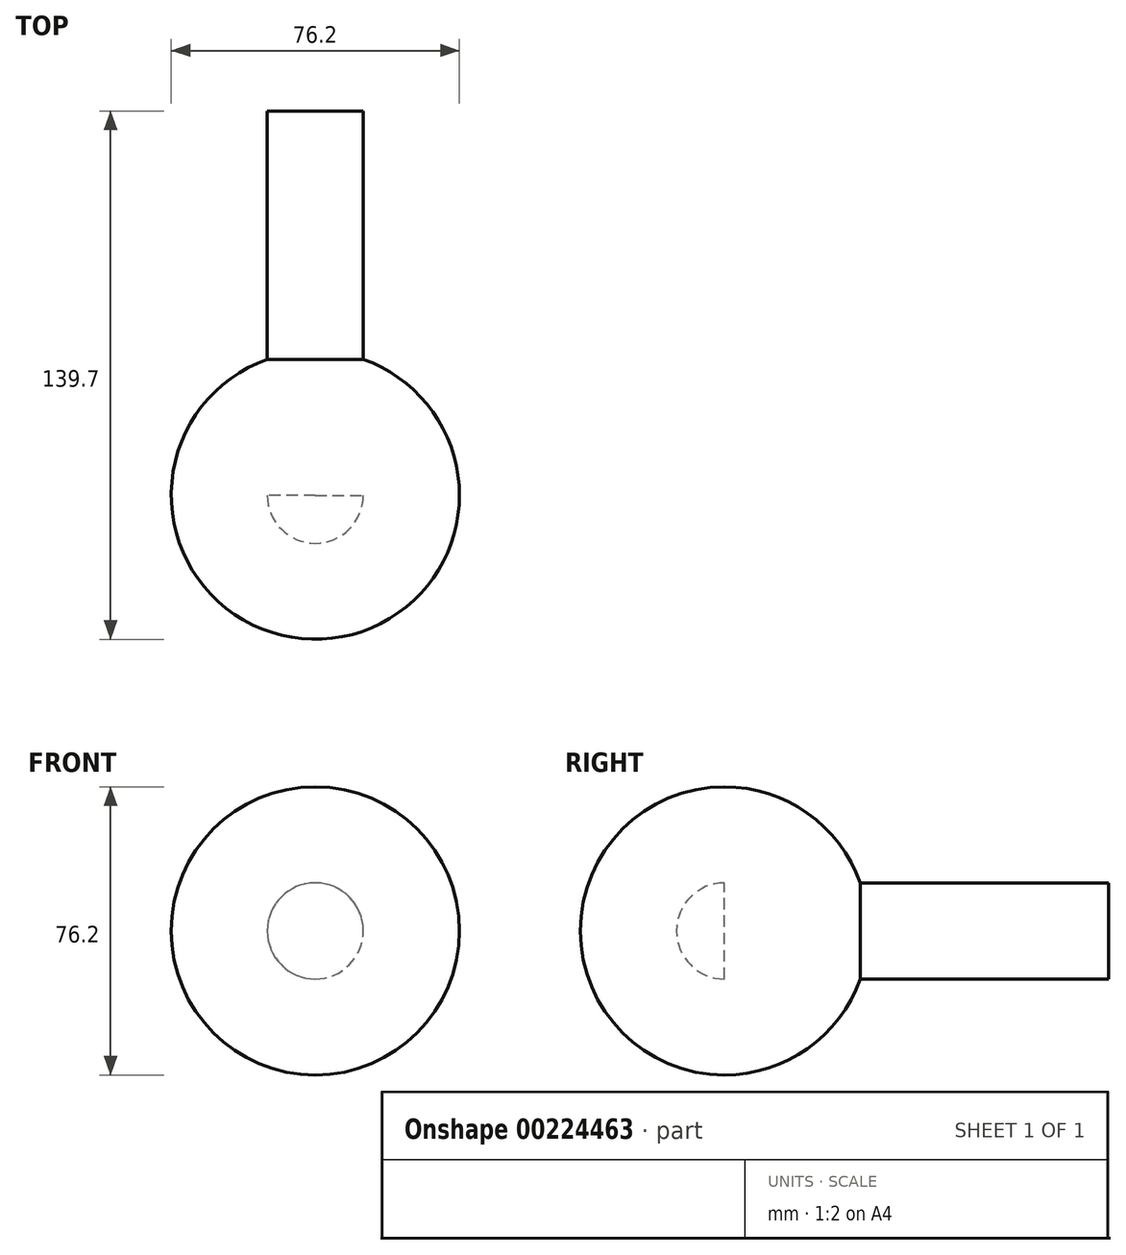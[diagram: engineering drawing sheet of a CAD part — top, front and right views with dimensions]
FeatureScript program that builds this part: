
annotation { "Feature Type Name" : "Feature", "Feature Type Description" : "" }
export const myFeature = defineFeature(function(context is Context, id is Id, definition is map)
    precondition{}
    {
        {
            var Q0;
            Q0=qCreatedBy(makeId("Front.planeOp"),FACE);
            var sketch = newSketch(context, id + "F0", { "sketchPlane" : qUnion([Q0])});
            skCircle(sketch, "E0", {"center": v(0, 0) * mm, "radius": 12.7 * mm});
            skSolve(sketch);
        }
        {
            var Q0;
            Q0 = qSketchRegion(id + "F0", true);
            extrude(context, id + "F1", {"entities" : qUnion([Q0]), "depth" : 101.6 * mm});
        }
        {
            var Q0;
            Q0=makeQuery(id+"F1.opExtrude","CAP_FACE",FACE,{"disambiguationData":[OSD([sQuery(id+"F0.wireOp",EDGE,"E0")])],"isStart":false});
            var sketch = newSketch(context, id + "F2", { "sketchPlane" : qUnion([Q0])});
            skCircle(sketch, "E1", {"center": v(0, 0) * mm, "radius": 38.1 * mm});
            skLineSegment(sketch, "E2", {"start": v(0, 38.1) * mm, "end": v(0, -38.1) * mm});
            skSolve(sketch);
        }
        {
            var Q0;
            {var subQ0=sQuery(id+"F2.wireOp",EDGE,"E2");var subQ1=sQuery(id+"F2.wireOp",EDGE,"E1");var subQ2=makeQuery(id+"F2.imprint","INTERSECT",VERTEX,{"disambiguationData":[OD(0.0)],"derivedFrom":[subQ1,subQ0]});Q0=makeQuery(id+"F2.imprint","IMPRINT",FACE,{"disambiguationData":[TD([[makeQuery(id+"F2.imprint","IMPRINT",EDGE,{"disambiguationData":[TD([[subQ2,1.0]])],"derivedFrom":subQ1}),1.0]])]});}
            var Q1;
            {var subQ0=sQuery(id+"F2.wireOp",EDGE,"E2");var subQ1=makeQuery(id+"F1.opExtrude","CAP_EDGE",EDGE,{"disambiguationData":[OSD([sQuery(id+"F0.wireOp",EDGE,"E0")])],"isStart":false});var subQ2=makeQuery(id+"F2.imprint","INTERSECT",VERTEX,{"disambiguationData":[OD(0.0)],"derivedFrom":[subQ1,subQ0]});Q1=makeQuery(id+"F2.imprint","IMPRINT",FACE,{"disambiguationData":[TD([[makeQuery(id+"F2.imprint","IMPRINT",EDGE,{"disambiguationData":[TD([[subQ2,-1.0]])],"derivedFrom":subQ0}),-1.0]])]});}
            var Q2;
            {var subQ0=sQuery(id+"F2.wireOp",EDGE,"E2");var subQ1=makeQuery(id+"F1.opExtrude","CAP_EDGE",EDGE,{"disambiguationData":[OSD([sQuery(id+"F0.wireOp",EDGE,"E0")])],"isStart":false});var subQ2=makeQuery(id+"F2.imprint","INTERSECT",VERTEX,{"disambiguationData":[OD(0.0)],"derivedFrom":[subQ1,subQ0]});Q2=makeQuery(id+"F2.imprint","IMPRINT",FACE,{"disambiguationData":[TD([[makeQuery(id+"F2.imprint","IMPRINT",EDGE,{"disambiguationData":[TD([[subQ2,-1.0]])],"derivedFrom":subQ0}),1.0]])]});}
            var Q3;
            Q3=sQuery(id+"F2.wireOp",EDGE,"E2");
            revolve(context, id + "F3", {"operationType" : NewBodyOperationType.ADD, "entities" : qUnion([Q0, Q1, Q2]), "axis" : qUnion([Q3]), "revolveType" : RevolveType.FULL});
        }
    });
